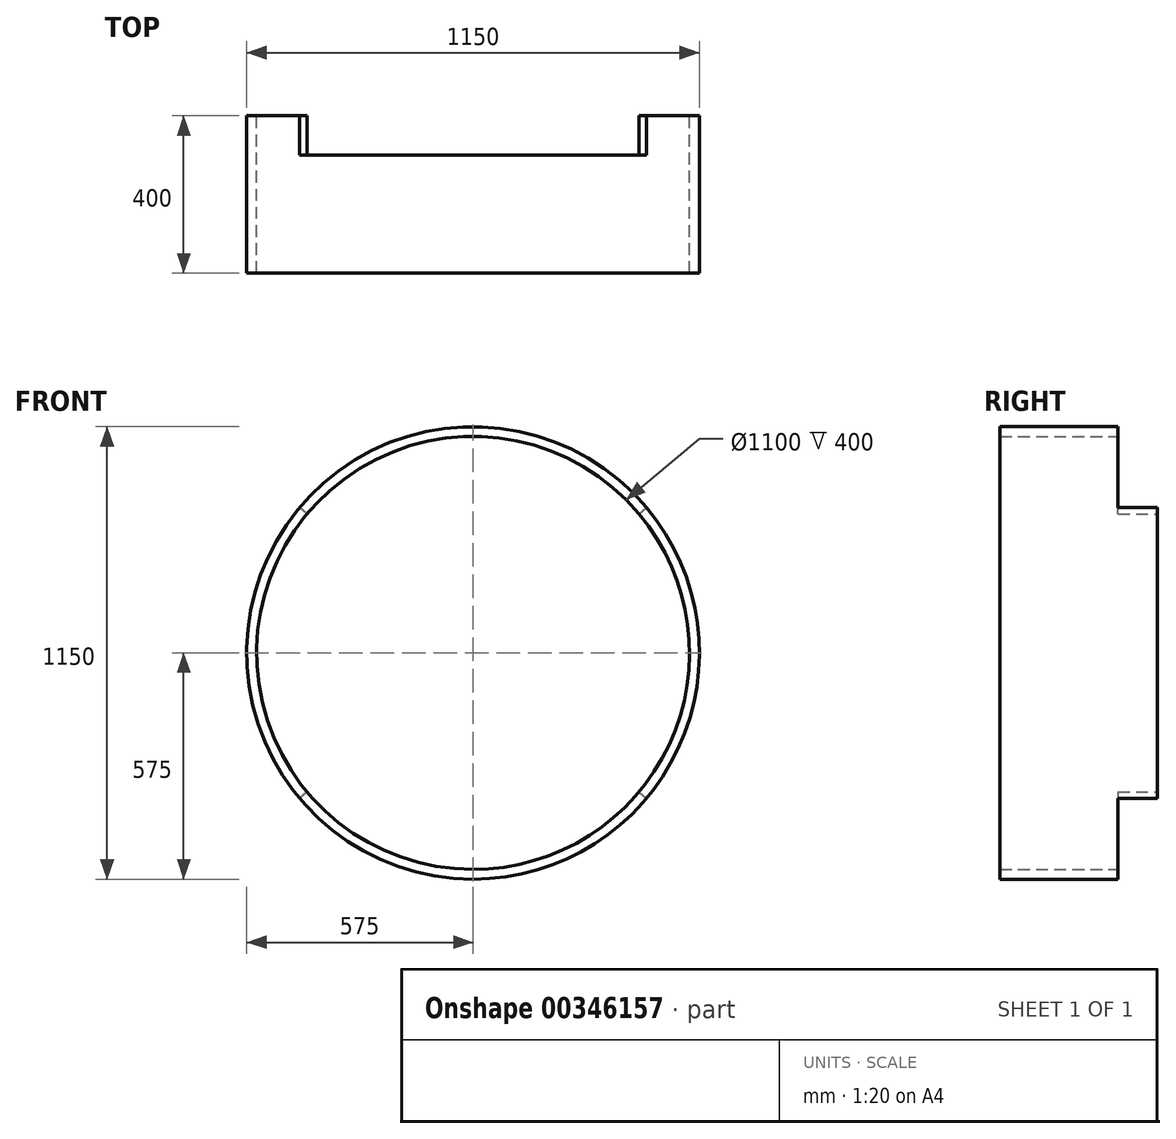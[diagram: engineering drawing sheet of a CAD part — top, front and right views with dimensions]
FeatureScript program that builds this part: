
annotation { "Feature Type Name" : "Feature", "Feature Type Description" : "" }
export const myFeature = defineFeature(function(context is Context, id is Id, definition is map)
    precondition{}
    {
        {
            var Q0;
            Q0=qCreatedBy(makeId("Front.planeOp"),FACE);
            var sketch = newSketch(context, id + "F0", { "sketchPlane" : qUnion([Q0])});
            skCircle(sketch, "E0", {"center": v(0, 0) * mm, "radius": 575 * mm});
            skCircle(sketch, "E1", {"center": v(0, 0) * mm, "radius": 550 * mm});
            skSolve(sketch);
        }
        {
            var Q0;
            Q0=makeQuery(id+"F0.imprint","IMPRINT",FACE,{"disambiguationData":[TD([[makeQuery(id+"F0.imprint","IMPRINT",EDGE,{"derivedFrom":sQuery(id+"F0.wireOp",EDGE,"E0")}),1.0]])]});
            extrude(context, id + "F1", {"entities" : qUnion([Q0]), "depth" : 400 * mm});
        }
        {
            var Q0;
            Q0=qCreatedBy(makeId("Front.planeOp"),FACE);
            var sketch = newSketch(context, id + "F2", { "sketchPlane" : qUnion([Q0])});
            skCircle(sketch, "E2.0", {"center": v(0, 0) * mm, "radius": 550 * mm});
            skCircle(sketch, "E3", {"center": v(0, 0) * mm, "radius": 300 * mm});
            skSolve(sketch);
        }
        {
            var Q0;
            Q0=makeQuery(id+"F0.imprint","IMPRINT",FACE,{"disambiguationData":[TD([[makeQuery(id+"F0.imprint","IMPRINT",EDGE,{"derivedFrom":sQuery(id+"F0.wireOp",EDGE,"E0")}),1.0]])]});
            var sketch = newSketch(context, id + "F3", { "sketchPlane" : qUnion([Q0])});
            skLineSegment(sketch, "E4", {"start": v(0, 0) * mm, "end": v(-440.48, 369.6) * mm});
            skLineSegment(sketch, "E5", {"start": v(0, 0) * mm, "end": v(0, 574.04) * mm, "construction": true});
            skLineSegment(sketch, "E6.MirrorCS", {"start": v(0, 0) * mm, "end": v(440.48, 369.6) * mm});
            skLineSegment(sketch, "E7", {"start": v(0, 0) * mm, "end": v(-575, 0) * mm, "construction": true});
            skLineSegment(sketch, "E8.MirrorCS", {"start": v(0, 0) * mm, "end": v(-440.48, -369.6) * mm});
            skLineSegment(sketch, "E9.MirrorCS", {"start": v(0, 0) * mm, "end": v(440.48, -369.6) * mm});
            skSolve(sketch);
        }
        {
            var Q0;
            {var subQ0=sQuery(id+"F3.wireOp",EDGE,"E6.MirrorCS");var subQ1=sQuery(id+"F3.wireOp",EDGE,"E4");var subQ2=makeQuery(id+"F3.imprint","INTERSECT",VERTEX,{"derivedFrom":[subQ1,subQ0]});Q0=makeQuery(id+"F3.imprint","IMPRINT",FACE,{"disambiguationData":[TD([[makeQuery(id+"F3.imprint","IMPRINT",EDGE,{"disambiguationData":[TD([[subQ2,-1.0]])],"derivedFrom":subQ1}),-1.0]])]});}
            var Q1;
            {var subQ0=sQuery(id+"F3.wireOp",EDGE,"E4");var subQ1=makeQuery(id+"F0.imprint","IMPRINT",EDGE,{"derivedFrom":sQuery(id+"F0.wireOp",EDGE,"E0")});var subQ2=makeQuery(id+"F3.imprint","INTERSECT",VERTEX,{"derivedFrom":[subQ1,subQ0]});Q1=makeQuery(id+"F3.imprint","IMPRINT",FACE,{"disambiguationData":[TD([[makeQuery(id+"F3.imprint","IMPRINT",EDGE,{"disambiguationData":[TD([[subQ2,1.0]])],"derivedFrom":subQ0}),-1.0]])]});}
            var Q2;
            {var subQ0=sQuery(id+"F3.wireOp",EDGE,"E8.MirrorCS");var subQ1=makeQuery(id+"F0.imprint","IMPRINT",EDGE,{"derivedFrom":sQuery(id+"F0.wireOp",EDGE,"E0")});var subQ2=makeQuery(id+"F3.imprint","INTERSECT",VERTEX,{"derivedFrom":[subQ1,subQ0]});Q2=makeQuery(id+"F3.imprint","IMPRINT",FACE,{"disambiguationData":[TD([[makeQuery(id+"F3.imprint","IMPRINT",EDGE,{"disambiguationData":[TD([[subQ2,1.0]])],"derivedFrom":subQ0}),1.0]])]});}
            extrude(context, id + "F4", {"entities" : qUnion([Q0, Q1, Q2]), "operationType" : NewBodyOperationType.REMOVE, "depth" : 100 * mm});
        }
    });
